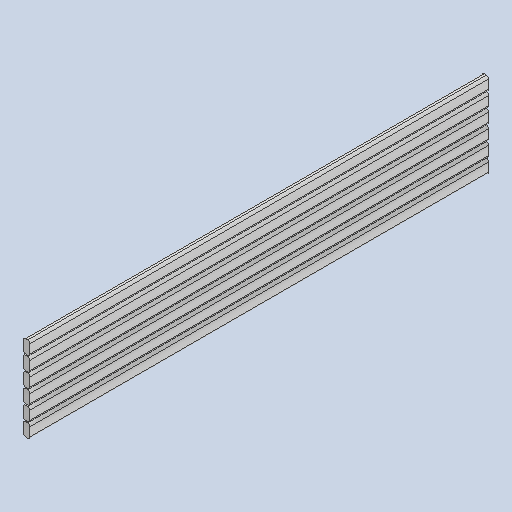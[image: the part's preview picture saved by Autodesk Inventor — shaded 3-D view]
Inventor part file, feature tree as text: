
AUTODESK INVENTOR PART (.ipt)
format: ipt  version: 2023 (Build 270158030, 158C)  size: 174,592 bytes
history: native  units: mm
features: other x4, extrude x1, sketch x1, reference x1
ambient origin geometry x8: Origin, YZ Plane, XZ Plane, XY Plane, X Axis, Y Axis, Z Axis, Center Point
bodies: Body1 (feature_tree)
feature tree (7):
  other  "slats"
  extrude  "Extrusion1"  [1 undecoded]
  sketch  "Sketch1"  dims[d0=2000.0mm d1=75.0mm d2=0.0mm d3=0.0mm]
  reference  "Reference1"
  other  "<userpath>\Documents\0004-inventor\3D-CAD-main\primary-engineer-bench.iam"
  other  "primary-engineer-bench.iam"
  other  "bench-end-peice:1"
note: 1 required parameter value undecoded (feature->parameter linkage not recoverable at this tier; creation-order binding heuristic only, values carry confidence <= 0.55)
